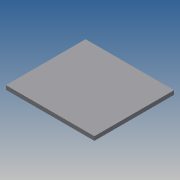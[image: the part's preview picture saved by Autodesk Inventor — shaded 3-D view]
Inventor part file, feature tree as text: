
AUTODESK INVENTOR PART (.ipt)
format: ipt  version: 2013 (Build 170138000, 138)  size: 66,048 bytes
history: native  units: mm
features: extrude x1, sketch x1
ambient origin geometry x8: Origin, YZ Plane, XZ Plane, XY Plane, X Axis, Y Axis, Z Axis, Center Point
bodies: Solid1 (feature_tree)
feature tree (2):
  extrude  "Extrusion1"  Depth=200.0mm
  sketch  "Sketch1"  dims[d0=222.0mm d1=200.0mm d2=10.0mm d3=0.0mm]
